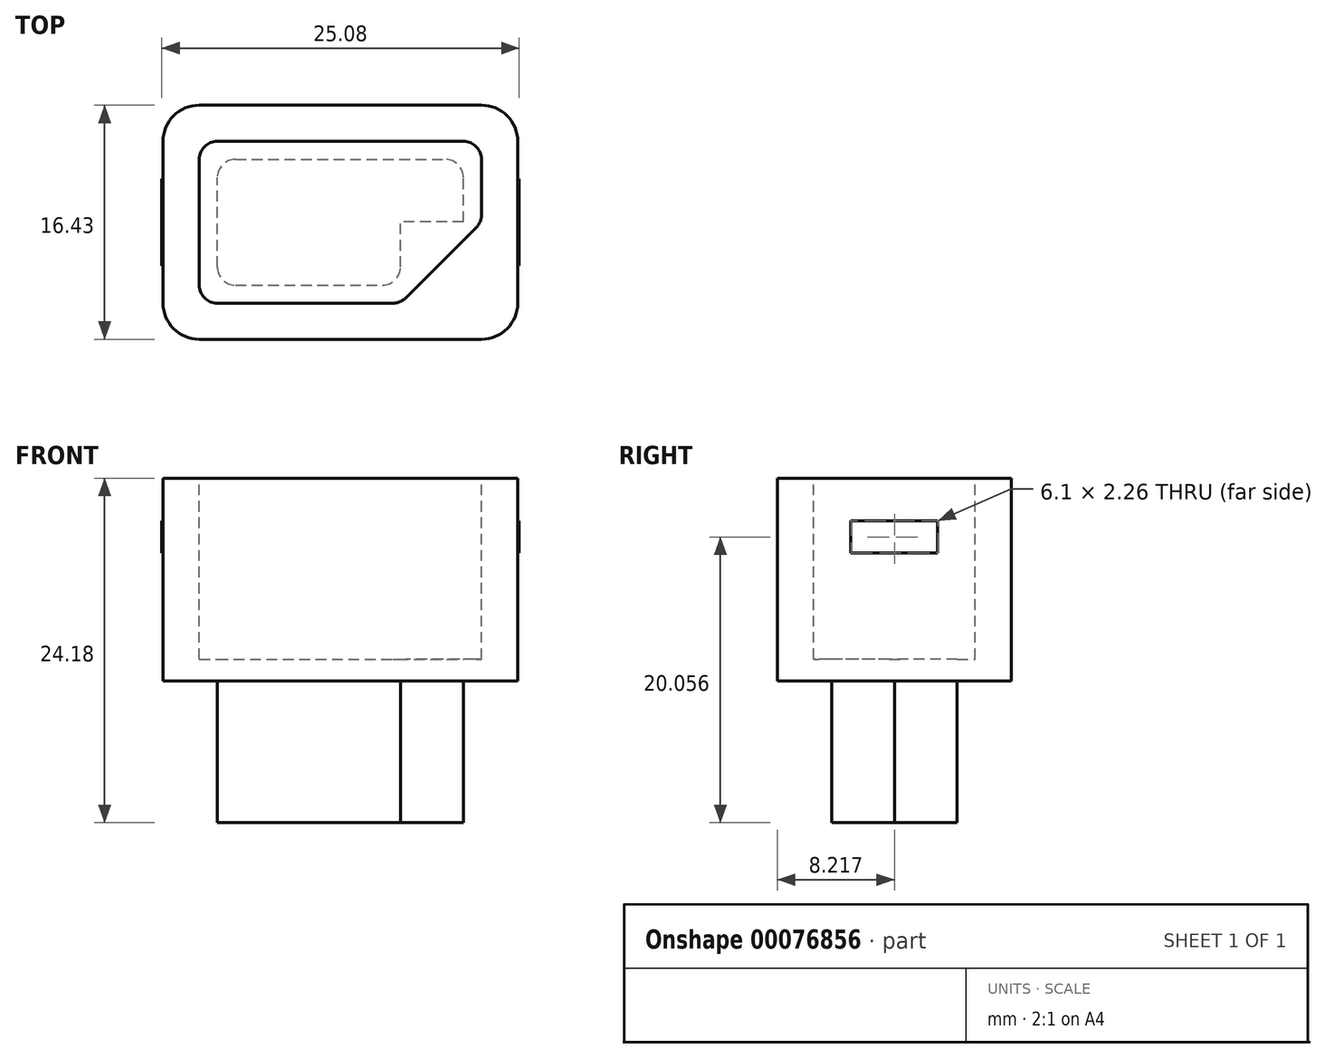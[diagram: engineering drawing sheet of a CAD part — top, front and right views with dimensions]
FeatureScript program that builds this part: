
annotation { "Feature Type Name" : "Feature", "Feature Type Description" : "" }
export const myFeature = defineFeature(function(context is Context, id is Id, definition is map)
    precondition{}
    {
        {
            var Q0;
            Q0=qCreatedBy(makeId("Top.planeOp"),FACE);
            var sketch = newSketch(context, id + "F0", { "sketchPlane" : qUnion([Q0])});
            skLineSegment(sketch, "E0.bottom", {"start": v(0, 0) * mm, "end": v(24.9, 0) * mm});
            skLineSegment(sketch, "E0.top", {"start": v(2.54, 16.43) * mm, "end": v(22.35, 16.43) * mm});
            skLineSegment(sketch, "E0.left", {"start": v(0, 2.54) * mm, "end": v(0, 13.9) * mm});
            skLineSegment(sketch, "E0.right", {"start": v(24.9, 2.54) * mm, "end": v(24.9, 13.9) * mm});
            skLineSegment(sketch, "E1.bottom", {"start": v(24.9, 0) * mm, "end": v(0, 0) * mm});
            skLineSegment(sketch, "E1.top", {"start": v(22.35, 0) * mm, "end": v(2.54, 0) * mm});
            skLineSegment(sketch, "E1.left", {"start": v(24.9, 0) * mm, "end": v(24.9, 0) * mm});
            skLineSegment(sketch, "E1.right", {"start": v(0, 0) * mm, "end": v(0, 0) * mm});
            skPoint(sketch, "E2.visualSharp", {"position": v(0, 16.43) * mm});
            skArc(sketch, "E2.filletArc", {"start": v(2.54, 16.43) * mm, "mid": v(0.74, 15.69) * mm, "end": v(0, 13.9) * mm});
            skPoint(sketch, "E3.visualSharp", {"position": v(24.9, 16.43) * mm});
            skArc(sketch, "E3.filletArc", {"start": v(24.9, 13.9) * mm, "mid": v(24.15, 15.69) * mm, "end": v(22.35, 16.43) * mm});
            skPoint(sketch, "E4.visualSharp", {"position": v(24.9, 0) * mm});
            skArc(sketch, "E4.filletArc", {"start": v(22.35, 0) * mm, "mid": v(24.15, 0.74) * mm, "end": v(24.9, 2.54) * mm});
            skPoint(sketch, "E5.visualSharp", {"position": v(0, 0) * mm});
            skArc(sketch, "E5.filletArc", {"start": v(0, 2.54) * mm, "mid": v(0.74, 0.74) * mm, "end": v(2.54, 0) * mm});
            skSolve(sketch);
        }
        {
            var Q0;
            Q0=makeQuery(id+"F0.imprint","IMPRINT",FACE,{"disambiguationData":[TD([[makeQuery(id+"F0.imprint","IMPRINT",EDGE,{"derivedFrom":sQuery(id+"F0.wireOp",EDGE,"E0.top")}),-1.0]])]});
            extrude(context, id + "F1", {"entities" : qUnion([Q0]), "depth" : 14.22 * mm});
        }
        {
            var Q0;
            Q0=makeQuery(id+"F1.opExtrude","SWEPT_FACE",FACE,{"disambiguationData":[OSD([sQuery(id+"F0.wireOp",EDGE,"E0.left")])]});
            var sketch = newSketch(context, id + "F2", { "sketchPlane" : qUnion([Q0])});
            skLineSegment(sketch, "E6.bottom", {"start": v(-13.9, 14.22) * mm, "end": v(-11.26, 14.22) * mm});
            skLineSegment(sketch, "E6.top", {"start": v(-13.9, 11.23) * mm, "end": v(-11.26, 11.23) * mm});
            skLineSegment(sketch, "E6.left", {"start": v(-13.9, 14.22) * mm, "end": v(-13.9, 11.23) * mm});
            skLineSegment(sketch, "E6.right", {"start": v(-11.26, 14.22) * mm, "end": v(-11.26, 11.23) * mm});
            skLineSegment(sketch, "E7.bottom", {"start": v(-11.26, 11.23) * mm, "end": v(-5.17, 11.23) * mm});
            skLineSegment(sketch, "E7.top", {"start": v(-11.26, 8.97) * mm, "end": v(-5.17, 8.97) * mm});
            skLineSegment(sketch, "E7.left", {"start": v(-11.26, 11.23) * mm, "end": v(-11.26, 8.97) * mm});
            skLineSegment(sketch, "E7.right", {"start": v(-5.17, 11.23) * mm, "end": v(-5.17, 8.97) * mm});
            skSolve(sketch);
        }
        {
            var Q0;
            Q0=makeQuery(id+"F2.imprint","IMPRINT",FACE,{"disambiguationData":[TD([[makeQuery(id+"F2.imprint","IMPRINT",EDGE,{"derivedFrom":sQuery(id+"F2.wireOp",EDGE,"E7.bottom")}),-1.0]])]});
            extrude(context, id + "F3", {"entities" : qUnion([Q0]), "operationType" : NewBodyOperationType.ADD, "depth" : ((1.17 - .98) / 2) * mm});
        }
        {
            var Q0;
            Q0=makeQuery(id+"F1.opExtrude","SWEPT_FACE",FACE,{"disambiguationData":[OSD([sQuery(id+"F0.wireOp",EDGE,"E0.right")])]});
            var sketch = newSketch(context, id + "F4", { "sketchPlane" : qUnion([Q0])});
            skLineSegment(sketch, "E8.bottom", {"start": v(13.9, 14.22) * mm, "end": v(11.25, 14.22) * mm, "construction": true});
            skLineSegment(sketch, "E8.top", {"start": v(13.9, 11.23) * mm, "end": v(11.25, 11.23) * mm, "construction": true});
            skLineSegment(sketch, "E8.left", {"start": v(13.9, 14.22) * mm, "end": v(13.9, 11.23) * mm, "construction": true});
            skLineSegment(sketch, "E8.right", {"start": v(11.25, 14.22) * mm, "end": v(11.25, 11.23) * mm, "construction": true});
            skLineSegment(sketch, "E9.bottom", {"start": v(11.25, 11.23) * mm, "end": v(5.16, 11.23) * mm});
            skLineSegment(sketch, "E9.top", {"start": v(11.25, 8.97) * mm, "end": v(5.16, 8.97) * mm});
            skLineSegment(sketch, "E9.left", {"start": v(11.25, 11.23) * mm, "end": v(11.25, 8.97) * mm});
            skLineSegment(sketch, "E9.right", {"start": v(5.16, 11.23) * mm, "end": v(5.16, 8.97) * mm});
            skSolve(sketch);
        }
        {
            var Q0;
            Q0=makeQuery(id+"F4.imprint","IMPRINT",FACE,{"disambiguationData":[TD([[makeQuery(id+"F4.imprint","IMPRINT",EDGE,{"derivedFrom":sQuery(id+"F4.wireOp",EDGE,"E9.bottom")}),1.0]])]});
            extrude(context, id + "F5", {"entities" : qUnion([Q0]), "operationType" : NewBodyOperationType.ADD, "depth" : ((1.17 - .98) / 2) * mm});
        }
        {
            var Q0;
            Q0=makeQuery(id+"F1.opExtrude","CAP_FACE",FACE,{"disambiguationData":[OSD([sQuery(id+"F0.wireOp",EDGE,"E0.top"),sQuery(id+"F0.wireOp",EDGE,"E0.left"),sQuery(id+"F0.wireOp",EDGE,"E0.right"),sQuery(id+"F0.wireOp",EDGE,"E1.top"),sQuery(id+"F0.wireOp",EDGE,"E2.filletArc"),sQuery(id+"F0.wireOp",EDGE,"E3.filletArc"),sQuery(id+"F0.wireOp",EDGE,"E4.filletArc"),sQuery(id+"F0.wireOp",EDGE,"E5.filletArc")])],"isStart":false});
            var sketch = newSketch(context, id + "F6", { "sketchPlane" : qUnion([Q0])});
            skLineSegment(sketch, "E10", {"start": v(0, 2.54) * mm, "end": v(2.54, 2.54) * mm, "construction": true});
            skLineSegment(sketch, "E11", {"start": v(2.54, 2.54) * mm, "end": v(2.54, 13.9) * mm, "construction": true});
            skLineSegment(sketch, "E12", {"start": v(2.54, 13.9) * mm, "end": v(22.35, 13.9) * mm, "construction": true});
            skLineSegment(sketch, "E13", {"start": v(22.35, 13.9) * mm, "end": v(22.35, 8.22) * mm, "construction": true});
            skLineSegment(sketch, "E14", {"start": v(16.66, 2.54) * mm, "end": v(2.54, 2.54) * mm, "construction": true});
            skLineSegment(sketch, "E15.bottom", {"start": v(3.8, 13.9) * mm, "end": v(21.08, 13.9) * mm});
            skLineSegment(sketch, "E15.top", {"start": v(3.8, 2.54) * mm, "end": v(16.14, 2.54) * mm});
            skLineSegment(sketch, "E15.left", {"start": v(2.54, 12.62) * mm, "end": v(2.54, 3.81) * mm});
            skLineSegment(sketch, "E15.right", {"start": v(22.35, 12.62) * mm, "end": v(22.35, 8.74) * mm});
            skLineSegment(sketch, "E16", {"start": v(21.98, 7.84) * mm, "end": v(17.03, 2.91) * mm});
            skPoint(sketch, "E17.orphan", {"position": v(22.35, 2.54) * mm});
            skPoint(sketch, "E18.visualSharp", {"position": v(2.54, 13.9) * mm});
            skArc(sketch, "E18.filletArc", {"start": v(3.8, 13.9) * mm, "mid": v(2.91, 13.52) * mm, "end": v(2.54, 12.62) * mm});
            skPoint(sketch, "E19.visualSharp", {"position": v(2.54, 2.54) * mm});
            skArc(sketch, "E19.filletArc", {"start": v(2.54, 3.8) * mm, "mid": v(2.91, 2.91) * mm, "end": v(3.8, 2.54) * mm});
            skPoint(sketch, "E20.visualSharp", {"position": v(16.66, 2.54) * mm});
            skArc(sketch, "E20.filletArc", {"start": v(16.14, 2.54) * mm, "mid": v(16.62, 2.64) * mm, "end": v(17.03, 2.91) * mm});
            skPoint(sketch, "E21.visualSharp", {"position": v(22.35, 8.22) * mm});
            skArc(sketch, "E21.filletArc", {"start": v(21.98, 7.84) * mm, "mid": v(22.26, 8.26) * mm, "end": v(22.35, 8.74) * mm});
            skPoint(sketch, "E22.visualSharp", {"position": v(22.35, 13.9) * mm});
            skArc(sketch, "E22.filletArc", {"start": v(22.35, 12.62) * mm, "mid": v(21.98, 13.52) * mm, "end": v(21.08, 13.9) * mm});
            skSolve(sketch);
        }
        {
            var Q0;
            Q0=makeQuery(id+"F6.imprint","IMPRINT",FACE,{"disambiguationData":[TD([[makeQuery(id+"F6.imprint","IMPRINT",EDGE,{"derivedFrom":sQuery(id+"F6.wireOp",EDGE,"E15.bottom")}),-1.0]])]});
            extrude(context, id + "F7", {"entities" : qUnion([Q0]), "operationType" : NewBodyOperationType.REMOVE, "oppositeDirection" : true, "depth" : 12.7 * mm});
        }
        {
            var Q0;
            Q0=makeQuery(id+"F1.opExtrude","CAP_FACE",FACE,{"disambiguationData":[OSD([sQuery(id+"F0.wireOp",EDGE,"E0.top"),sQuery(id+"F0.wireOp",EDGE,"E0.left"),sQuery(id+"F0.wireOp",EDGE,"E0.right"),sQuery(id+"F0.wireOp",EDGE,"E1.top"),sQuery(id+"F0.wireOp",EDGE,"E2.filletArc"),sQuery(id+"F0.wireOp",EDGE,"E3.filletArc"),sQuery(id+"F0.wireOp",EDGE,"E4.filletArc"),sQuery(id+"F0.wireOp",EDGE,"E5.filletArc")])],"isStart":true});
            var sketch = newSketch(context, id + "F8", { "sketchPlane" : qUnion([Q0])});
            skLineSegment(sketch, "E23", {"start": v(2.54, 0) * mm, "end": v(2.54, -2.54) * mm, "construction": true});
            skLineSegment(sketch, "E24", {"start": v(2.54, -2.54) * mm, "end": v(3.8, -2.54) * mm, "construction": true});
            skLineSegment(sketch, "E25", {"start": v(3.8, -2.54) * mm, "end": v(3.8, -3.81) * mm, "construction": true});
            skLineSegment(sketch, "E26", {"start": v(22.35, -16.43) * mm, "end": v(22.35, -13.9) * mm, "construction": true});
            skLineSegment(sketch, "E27", {"start": v(22.35, -13.9) * mm, "end": v(21.08, -13.9) * mm, "construction": true});
            skLineSegment(sketch, "E28", {"start": v(21.08, -13.9) * mm, "end": v(21.08, -12.62) * mm, "construction": true});
            skLineSegment(sketch, "E29.bottom", {"start": v(5.08, -3.81) * mm, "end": v(15.4, -3.81) * mm});
            skLineSegment(sketch, "E29.top", {"start": v(5.08, -12.62) * mm, "end": v(19.81, -12.62) * mm});
            skLineSegment(sketch, "E29.left", {"start": v(3.8, -5.08) * mm, "end": v(3.8, -11.35) * mm});
            skPoint(sketch, "E30.oppositeSnap0", {"position": v(21.08, -8.24) * mm});
            skLineSegment(sketch, "E30.top", {"start": v(21.08, -8.24) * mm, "end": v(16.68, -8.24) * mm});
            skLineSegment(sketch, "E30.right", {"start": v(16.68, -5.08) * mm, "end": v(16.68, -8.24) * mm});
            skPoint(sketch, "E31.visualSharp", {"position": v(21.08, -12.62) * mm});
            skArc(sketch, "E31.filletArc", {"start": v(19.81, -12.62) * mm, "mid": v(20.71, -12.25) * mm, "end": v(21.08, -11.35) * mm});
            skPoint(sketch, "E32.visualSharp", {"position": v(3.8, -12.62) * mm});
            skArc(sketch, "E32.filletArc", {"start": v(3.8, -11.35) * mm, "mid": v(4.18, -12.25) * mm, "end": v(5.08, -12.62) * mm});
            skPoint(sketch, "E33.visualSharp", {"position": v(3.8, -3.81) * mm});
            skArc(sketch, "E33.filletArc", {"start": v(5.08, -3.81) * mm, "mid": v(4.18, -4.18) * mm, "end": v(3.8, -5.08) * mm});
            skArc(sketch, "E34.filletArc", {"start": v(16.68, -5.08) * mm, "mid": v(16.3, -4.18) * mm, "end": v(15.4, -3.81) * mm});
            skLineSegment(sketch, "E35", {"start": v(21.08, -8.24) * mm, "end": v(21.08, -11.35) * mm});
            skSolve(sketch);
        }
        {
            var Q0;
            Q0=makeQuery(id+"F8.imprint","IMPRINT",FACE,{"disambiguationData":[TD([[makeQuery(id+"F8.imprint","IMPRINT",EDGE,{"derivedFrom":sQuery(id+"F8.wireOp",EDGE,"E29.bottom")}),-1.0]])]});
            extrude(context, id + "F9", {"entities" : qUnion([Q0]), "operationType" : NewBodyOperationType.ADD, "depth" : 9.96 * mm});
        }
    });
